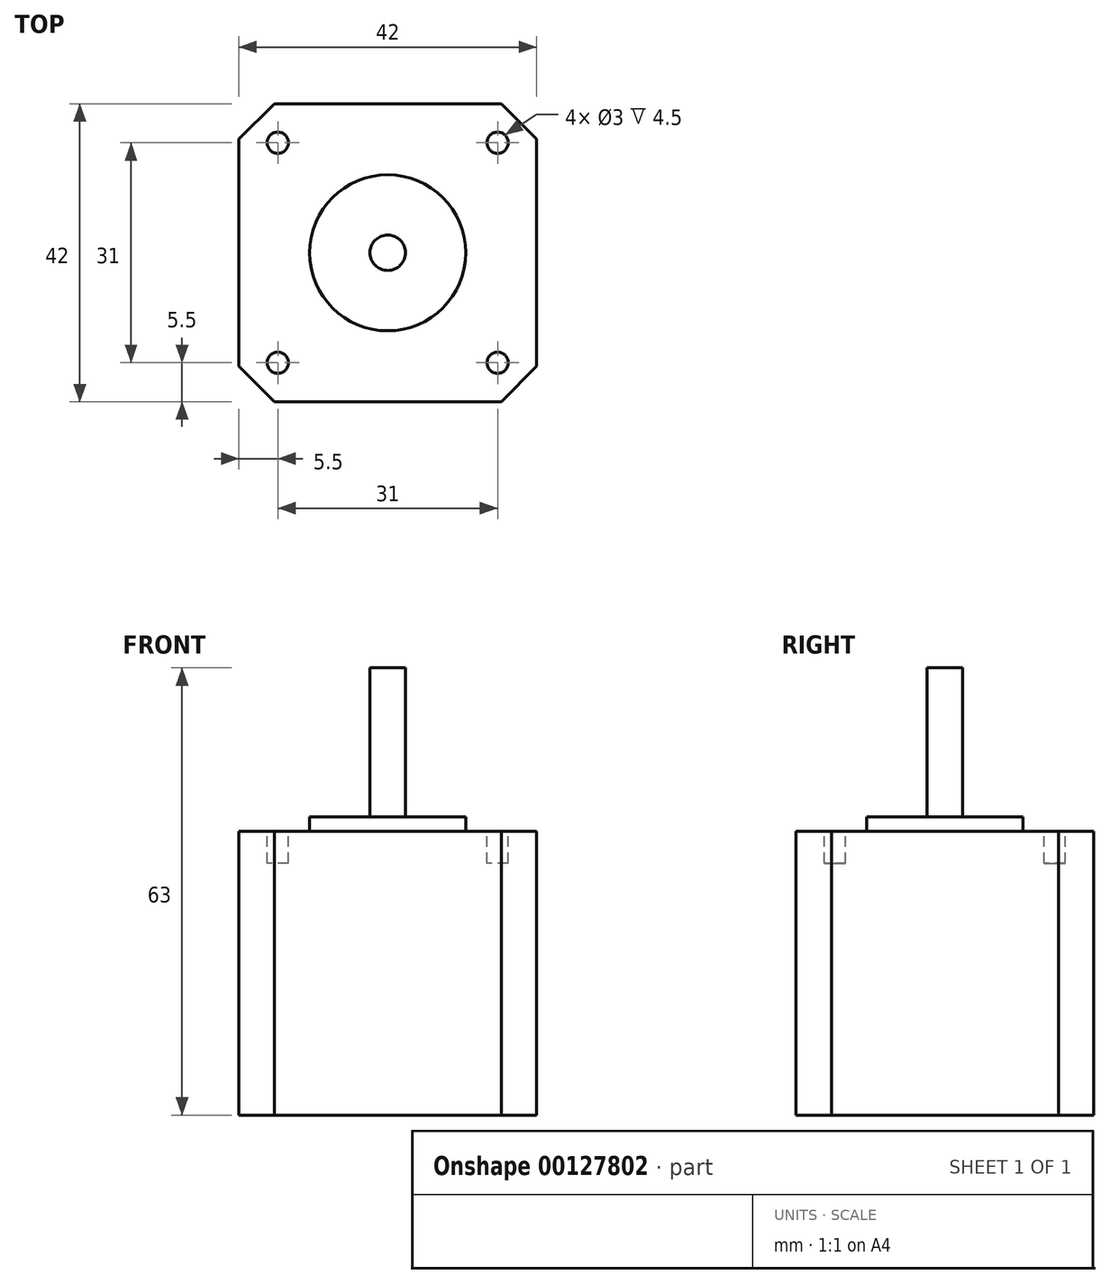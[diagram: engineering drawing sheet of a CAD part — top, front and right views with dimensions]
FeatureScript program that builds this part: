
annotation { "Feature Type Name" : "Feature", "Feature Type Description" : "" }
export const myFeature = defineFeature(function(context is Context, id is Id, definition is map)
    precondition{}
    {
        {
            var Q0;
            Q0=qCreatedBy(makeId("Top.planeOp"),FACE);
            var sketch = newSketch(context, id + "F0", { "sketchPlane" : qUnion([Q0])});
            skLineSegment(sketch, "E0.bottom", {"start": v(21, -21) * mm, "end": v(-21, -21) * mm});
            skLineSegment(sketch, "E0.top", {"start": v(21, 21) * mm, "end": v(-21, 21) * mm});
            skLineSegment(sketch, "E0.left", {"start": v(21, -21) * mm, "end": v(21, 21) * mm});
            skLineSegment(sketch, "E0.right", {"start": v(-21, -21) * mm, "end": v(-21, 21) * mm});
            skPoint(sketch, "E0.middle", {"position": v(0, 0) * mm});
            skSolve(sketch);
        }
        {
            var Q0;
            Q0=makeQuery(id+"F0.imprint","IMPRINT",FACE,{"disambiguationData":[TD([[makeQuery(id+"F0.imprint","IMPRINT",EDGE,{"derivedFrom":sQuery(id+"F0.wireOp",EDGE,"E0.bottom")}),-1.0]])]});
            extrude(context, id + "F1", {"entities" : qUnion([Q0]), "depth" : 40 * mm});
        }
        {
            var Q0;
            Q0=makeQuery(id+"F1.opExtrude","CAP_FACE",FACE,{"disambiguationData":[OSD([sQuery(id+"F0.wireOp",EDGE,"E0.bottom"),sQuery(id+"F0.wireOp",EDGE,"E0.top"),sQuery(id+"F0.wireOp",EDGE,"E0.left"),sQuery(id+"F0.wireOp",EDGE,"E0.right")])],"isStart":false});
            var sketch = newSketch(context, id + "F2", { "sketchPlane" : qUnion([Q0])});
            skCircle(sketch, "E1", {"center": v(0, 0) * mm, "radius": 11 * mm});
            skSolve(sketch);
        }
        {
            var Q0;
            Q0 = qSketchRegion(id + "F2", true);
            extrude(context, id + "F3", {"entities" : qUnion([Q0]), "operationType" : NewBodyOperationType.ADD, "depth" : 2 * mm});
        }
        {
            var Q0;
            Q0=makeQuery(id+"F3.opExtrude","CAP_FACE",FACE,{"disambiguationData":[OSD([sQuery(id+"F2.wireOp",EDGE,"E1")])],"isStart":false});
            var sketch = newSketch(context, id + "F4", { "sketchPlane" : qUnion([Q0])});
            skCircle(sketch, "E2", {"center": v(0, 0) * mm, "radius": 2.5 * mm});
            skSolve(sketch);
        }
        {
            var Q0;
            Q0 = qSketchRegion(id + "F4", true);
            extrude(context, id + "F5", {"entities" : qUnion([Q0]), "operationType" : NewBodyOperationType.ADD, "depth" : 21 * mm});
        }
        {
            var Q0;
            Q0=makeQuery(id+"F1.opExtrude","CAP_FACE",FACE,{"disambiguationData":[OSD([sQuery(id+"F0.wireOp",EDGE,"E0.bottom"),sQuery(id+"F0.wireOp",EDGE,"E0.top"),sQuery(id+"F0.wireOp",EDGE,"E0.left"),sQuery(id+"F0.wireOp",EDGE,"E0.right")])],"isStart":false});
            var sketch = newSketch(context, id + "F6", { "sketchPlane" : qUnion([Q0])});
            skCircle(sketch, "E3", {"center": v(-15.5, 15.5) * mm, "radius": 1.5 * mm});
            skLineSegment(sketch, "E4", {"start": v(-38.13, 0) * mm, "end": v(0, 0) * mm, "construction": true});
            skLineSegment(sketch, "E5", {"start": v(0, 0) * mm, "end": v(0, 46.17) * mm, "construction": true});
            skCircle(sketch, "E6.MirrorC", {"center": v(-15.5, -15.5) * mm, "radius": 1.5 * mm});
            skCircle(sketch, "E7.MirrorC", {"center": v(15.5, 15.5) * mm, "radius": 1.5 * mm});
            skCircle(sketch, "E8.MirrorC", {"center": v(15.5, -15.5) * mm, "radius": 1.5 * mm});
            skSolve(sketch);
        }
        {
            var Q0;
            Q0 = qSketchRegion(id + "F6", true);
            extrude(context, id + "F7", {"entities" : qUnion([Q0]), "operationType" : NewBodyOperationType.REMOVE, "oppositeDirection" : true, "depth" : 4.5 * mm});
        }
        {
            var Q0;
            Q0=makeQuery(id+"F1.opExtrude","SWEPT_EDGE",EDGE,{"disambiguationData":[OSD([sQuery(id+"F0.wireOp",EDGE,"E0.top"),sQuery(id+"F0.wireOp",EDGE,"E0.left")])]});
            var Q1;
            Q1=makeQuery(id+"F1.opExtrude","SWEPT_EDGE",EDGE,{"disambiguationData":[OSD([sQuery(id+"F0.wireOp",EDGE,"E0.bottom"),sQuery(id+"F0.wireOp",EDGE,"E0.left")])]});
            var Q2;
            Q2=makeQuery(id+"F1.opExtrude","SWEPT_EDGE",EDGE,{"disambiguationData":[OSD([sQuery(id+"F0.wireOp",EDGE,"E0.bottom"),sQuery(id+"F0.wireOp",EDGE,"E0.right")])]});
            var Q3;
            Q3=makeQuery(id+"F1.opExtrude","SWEPT_EDGE",EDGE,{"disambiguationData":[OSD([sQuery(id+"F0.wireOp",EDGE,"E0.top"),sQuery(id+"F0.wireOp",EDGE,"E0.right")])]});
            chamfer(context, id + "F8", {"entities" : qUnion([Q0, Q1, Q2, Q3]), "width" : 5 * mm, "tangentPropagation" : true});
        }
    });
